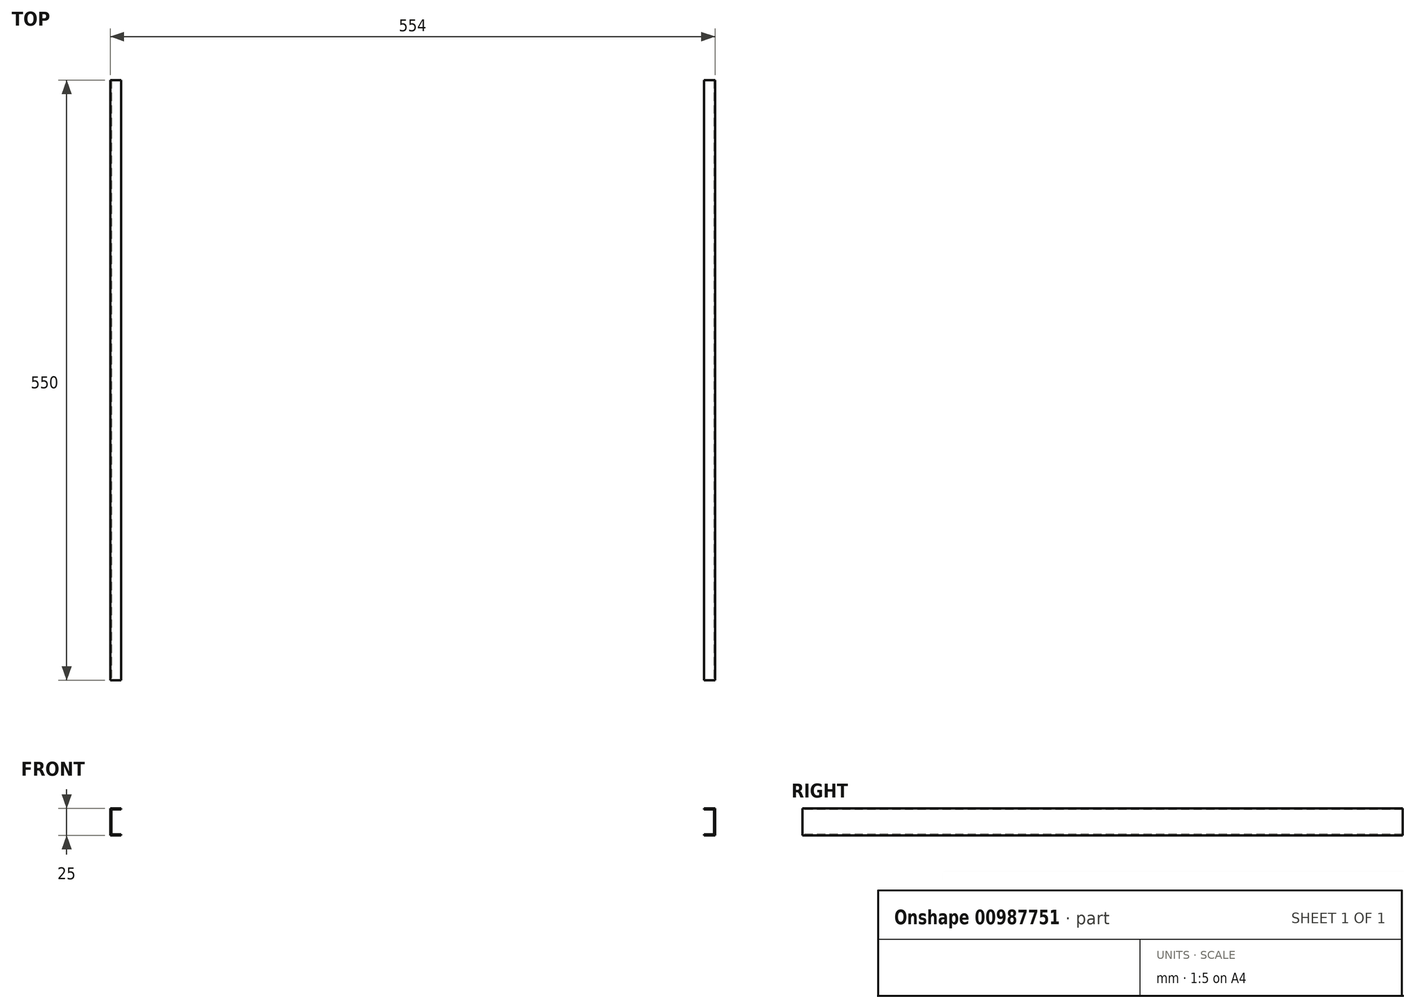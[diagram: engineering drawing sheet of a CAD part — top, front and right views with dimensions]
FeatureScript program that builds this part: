
annotation { "Feature Type Name" : "Feature", "Feature Type Description" : "" }
export const myFeature = defineFeature(function(context is Context, id is Id, definition is map)
    precondition{}
    {
        {
            var Q0;
            Q0=qCreatedBy(makeId("Front.planeOp"),FACE);
            var sketch = newSketch(context, id + "F0", { "sketchPlane" : qUnion([Q0])});
            skLineSegment(sketch, "E0.bottom", {"start": v(-277, 29.83) * mm, "end": v(-267, 29.83) * mm});
            skLineSegment(sketch, "E0.top", {"start": v(-277, 4.83) * mm, "end": v(-267, 4.83) * mm});
            skLineSegment(sketch, "E0.left", {"start": v(-277, 29.83) * mm, "end": v(-277, 4.83) * mm});
            skLineSegment(sketch, "E1.0", {"start": v(-276, 28.83) * mm, "end": v(-267, 28.83) * mm});
            skLineSegment(sketch, "E1.1", {"start": v(-276, 28.83) * mm, "end": v(-276, 5.83) * mm});
            skLineSegment(sketch, "E1.2", {"start": v(-276, 5.83) * mm, "end": v(-267, 5.83) * mm});
            skLineSegment(sketch, "E2", {"start": v(-267, 29.83) * mm, "end": v(-267, 28.83) * mm});
            skLineSegment(sketch, "E3", {"start": v(-267, 4.83) * mm, "end": v(-267, 5.83) * mm});
            skSolve(sketch);
        }
        {
            var Q0;
            Q0=makeQuery(id+"F0.imprint","IMPRINT",FACE,{"disambiguationData":[TD([[makeQuery(id+"F0.imprint","IMPRINT",EDGE,{"derivedFrom":sQuery(id+"F0.wireOp",EDGE,"E0.bottom")}),-1.0]])]});
            extrude(context, id + "F1", {"entities" : qUnion([Q0]), "oppositeDirection" : true, "depth" : 550 * mm, "offsetDistance" : 25 * mm});
        }
        {
            var Q0;
            Q0=makeQuery(id+"F1.opExtrude","SWEPT_BODY",BODY,{"disambiguationData":[OSD([sQuery(id+"F0.wireOp",EDGE,"E0.bottom"),sQuery(id+"F0.wireOp",EDGE,"E0.top"),sQuery(id+"F0.wireOp",EDGE,"E0.left"),sQuery(id+"F0.wireOp",EDGE,"E1.0"),sQuery(id+"F0.wireOp",EDGE,"E1.1"),sQuery(id+"F0.wireOp",EDGE,"E1.2"),sQuery(id+"F0.wireOp",EDGE,"E2"),sQuery(id+"F0.wireOp",EDGE,"E3")])]});
            var Q1;
            Q1=qCreatedBy(makeId("Right.planeOp"),FACE);
            mirror(context, id + "F2", {"entities" : qUnion([Q0]), "mirrorPlane" : qUnion([Q1])});
        }
    });
